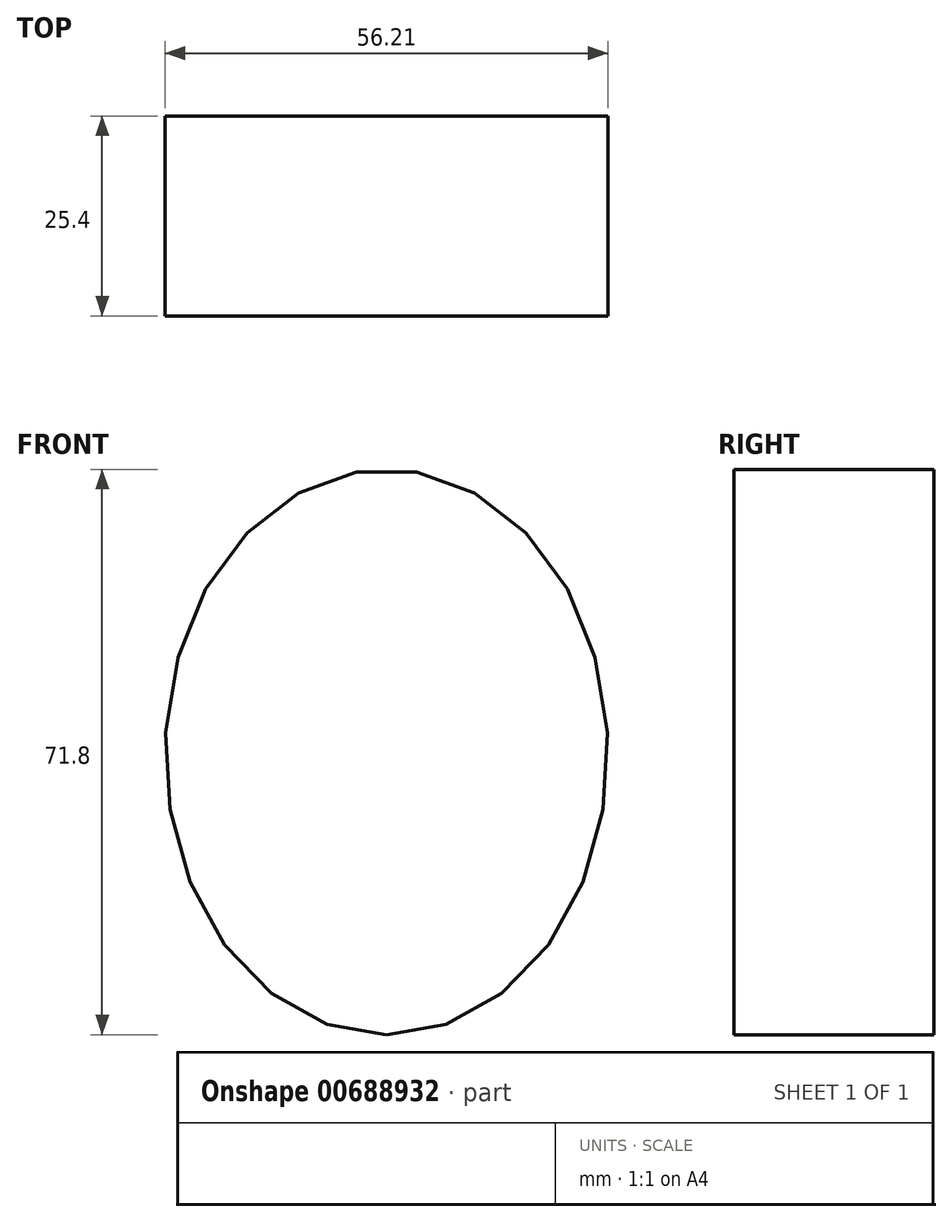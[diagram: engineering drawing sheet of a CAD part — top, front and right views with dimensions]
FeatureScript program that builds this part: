
annotation { "Feature Type Name" : "Feature", "Feature Type Description" : "" }
export const myFeature = defineFeature(function(context is Context, id is Id, definition is map)
    precondition{}
    {
        {
            var Q0;
            Q0=qCreatedBy(makeId("Front.planeOp"),FACE);
            var sketch = newSketch(context, id + "F0", { "sketchPlane" : qUnion([Q0])});
            skEllipse(sketch, "E0", {"center": v(-27.97, 39.05) * mm, "majorRadius": 35.9 * mm, "minorRadius": 28.1 * mm, "majorAxis": v(0, -1)});
            skSolve(sketch);
        }
        {
            var Q0;
            Q0=makeQuery(id+"F0.imprint","IMPRINT",FACE,{"disambiguationData":[TD([[makeQuery(id+"F0.imprint","IMPRINT",EDGE,{"derivedFrom":sQuery(id+"F0.wireOp",EDGE,"E0")}),1.0]])]});
            extrude(context, id + "F1", {"entities" : qUnion([Q0]), "depth" : 25.4 * mm, "offsetDistance" : 25.4 * mm});
        }
    });
